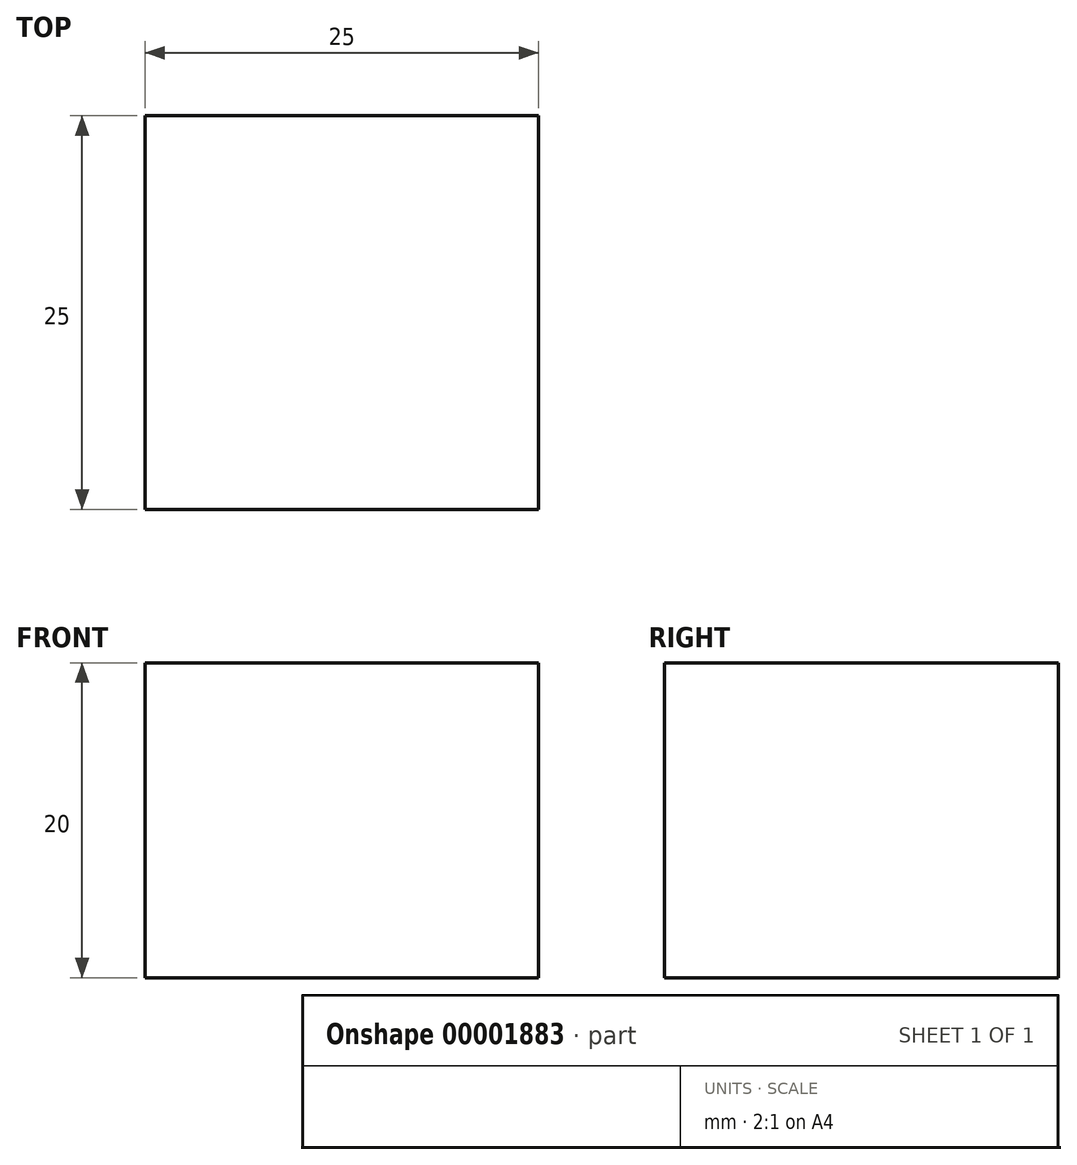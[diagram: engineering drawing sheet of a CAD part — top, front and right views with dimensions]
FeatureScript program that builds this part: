
annotation { "Feature Type Name" : "Feature", "Feature Type Description" : "" }
export const myFeature = defineFeature(function(context is Context, id is Id, definition is map)
    precondition{}
    {
        {
            var Q0;
            Q0=qCreatedBy(makeId("Top.planeOp"),FACE);
            var sketch = newSketch(context, id + "F0", { "sketchPlane" : qUnion([Q0])});
            skLineSegment(sketch, "E0.bottom", {"start": v(-10.1, 17.66) * mm, "end": v(14.9, 17.66) * mm});
            skLineSegment(sketch, "E0.top", {"start": v(-10.1, -7.34) * mm, "end": v(14.9, -7.34) * mm});
            skLineSegment(sketch, "E0.left", {"start": v(-10.1, 17.66) * mm, "end": v(-10.1, -7.34) * mm});
            skLineSegment(sketch, "E0.right", {"start": v(14.9, 17.66) * mm, "end": v(14.9, -7.34) * mm});
            skSolve(sketch);
        }
        {
            var Q0;
            Q0=makeQuery(id+"F0.imprint","IMPRINT",FACE,{"disambiguationData":[TD([[makeQuery(id+"F0.imprint","IMPRINT",EDGE,{"derivedFrom":sQuery(id+"F0.wireOp",EDGE,"E0.bottom")}),-1.0]])]});
            extrude(context, id + "F1", {"entities" : qUnion([Q0]), "depth" : 20 * mm, "offsetDistance" : 25 * mm});
        }
    });
